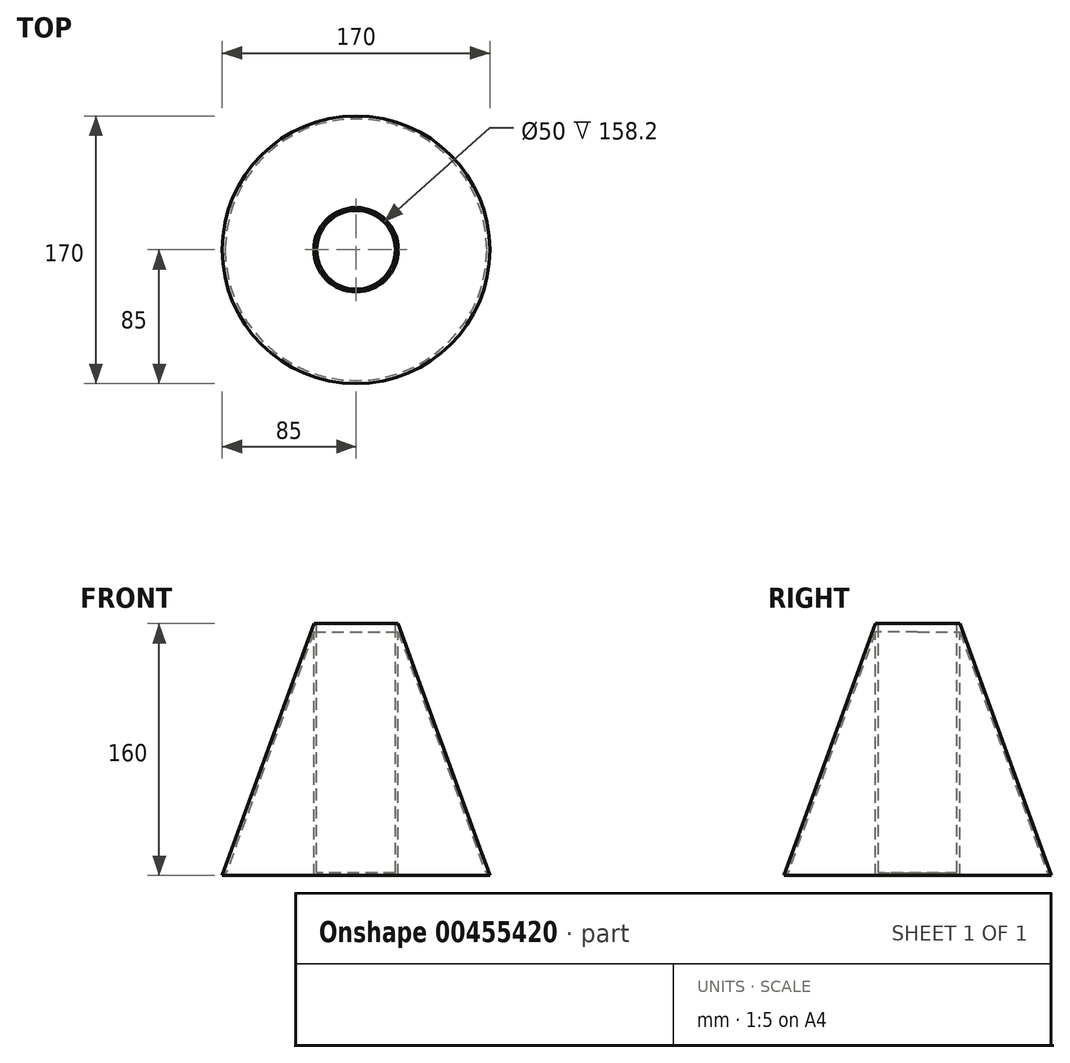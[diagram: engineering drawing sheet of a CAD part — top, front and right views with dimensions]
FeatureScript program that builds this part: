
annotation { "Feature Type Name" : "Feature", "Feature Type Description" : "" }
export const myFeature = defineFeature(function(context is Context, id is Id, definition is map)
    precondition{}
    {
        {
            var Q0;
            Q0=qCreatedBy(makeId("Top.planeOp"),FACE);
            var sketch = newSketch(context, id + "F0", { "sketchPlane" : qUnion([Q0])});
            skCircle(sketch, "E0", {"center": v(0, 0) * mm, "radius": 85 * mm});
            skSolve(sketch);
        }
        {
            var Q0;
            Q0=qCreatedBy(makeId("Top.planeOp"),FACE);
            cPlane(context, id + "F1", {"entities" : qUnion([Q0]), "cplaneType" : CPlaneType.OFFSET, "offset" : 160 * mm, "width" : 150 * mm, "height" : 150 * mm});
        }
        {
            var Q0;
            Q0=qCreatedBy(id+"F1.planeOp",FACE);
            var sketch = newSketch(context, id + "F2", { "sketchPlane" : qUnion([Q0])});
            skCircle(sketch, "E1", {"center": v(0, 0) * mm, "radius": 26.8 * mm});
            skSolve(sketch);
        }
        {
            var Q0;
            Q0=makeQuery(id+"F2.imprint","IMPRINT",FACE,{"disambiguationData":[TD([[makeQuery(id+"F2.imprint","IMPRINT",EDGE,{"derivedFrom":sQuery(id+"F2.wireOp",EDGE,"E1")}),1.0]])]});
            var Q1;
            Q1=makeQuery(id+"F0.imprint","IMPRINT",FACE,{"disambiguationData":[TD([[makeQuery(id+"F0.imprint","IMPRINT",EDGE,{"derivedFrom":sQuery(id+"F0.wireOp",EDGE,"E0")}),1.0]])]});
            loft(context, id + "F3", {"sheetProfilesArray" : [{ "sheetProfileEntities" : qUnion([Q0]) }, { "sheetProfileEntities" : qUnion([Q1]) }]});
        }
        {
            var Q0;
            Q0=qCreatedBy(id+"F1.planeOp",FACE);
            var sketch = newSketch(context, id + "F4", { "sketchPlane" : qUnion([Q0])});
            skCircle(sketch, "E2", {"center": v(0, 0) * mm, "radius": 25 * mm});
            skSolve(sketch);
        }
        {
            var Q0;
            Q0=makeQuery(id+"F4.imprint","IMPRINT",FACE,{"disambiguationData":[TD([[makeQuery(id+"F4.imprint","IMPRINT",EDGE,{"derivedFrom":sQuery(id+"F4.wireOp",EDGE,"E2")}),1.0]])]});
            extrude(context, id + "F5", {"entities" : qUnion([Q0]), "operationType" : NewBodyOperationType.REMOVE, "oppositeDirection" : true, "depth" : 158.2 * mm});
        }
        {
            var Q0;
            Q0=makeQuery(id+"F3.opLoft","CAP_FACE",FACE,{"disambiguationData":[OSD([makeQuery(id+"F0.imprint","IMPRINT",FACE,{"disambiguationData":[TD([[makeQuery(id+"F0.imprint","IMPRINT",EDGE,{"derivedFrom":sQuery(id+"F0.wireOp",EDGE,"E0")}),1.0]])]})])],"isStart":true});
            shell(context, id + "F6", {"entities" : qUnion([Q0]), "thickness" : 1.8 * mm});
        }
    });
